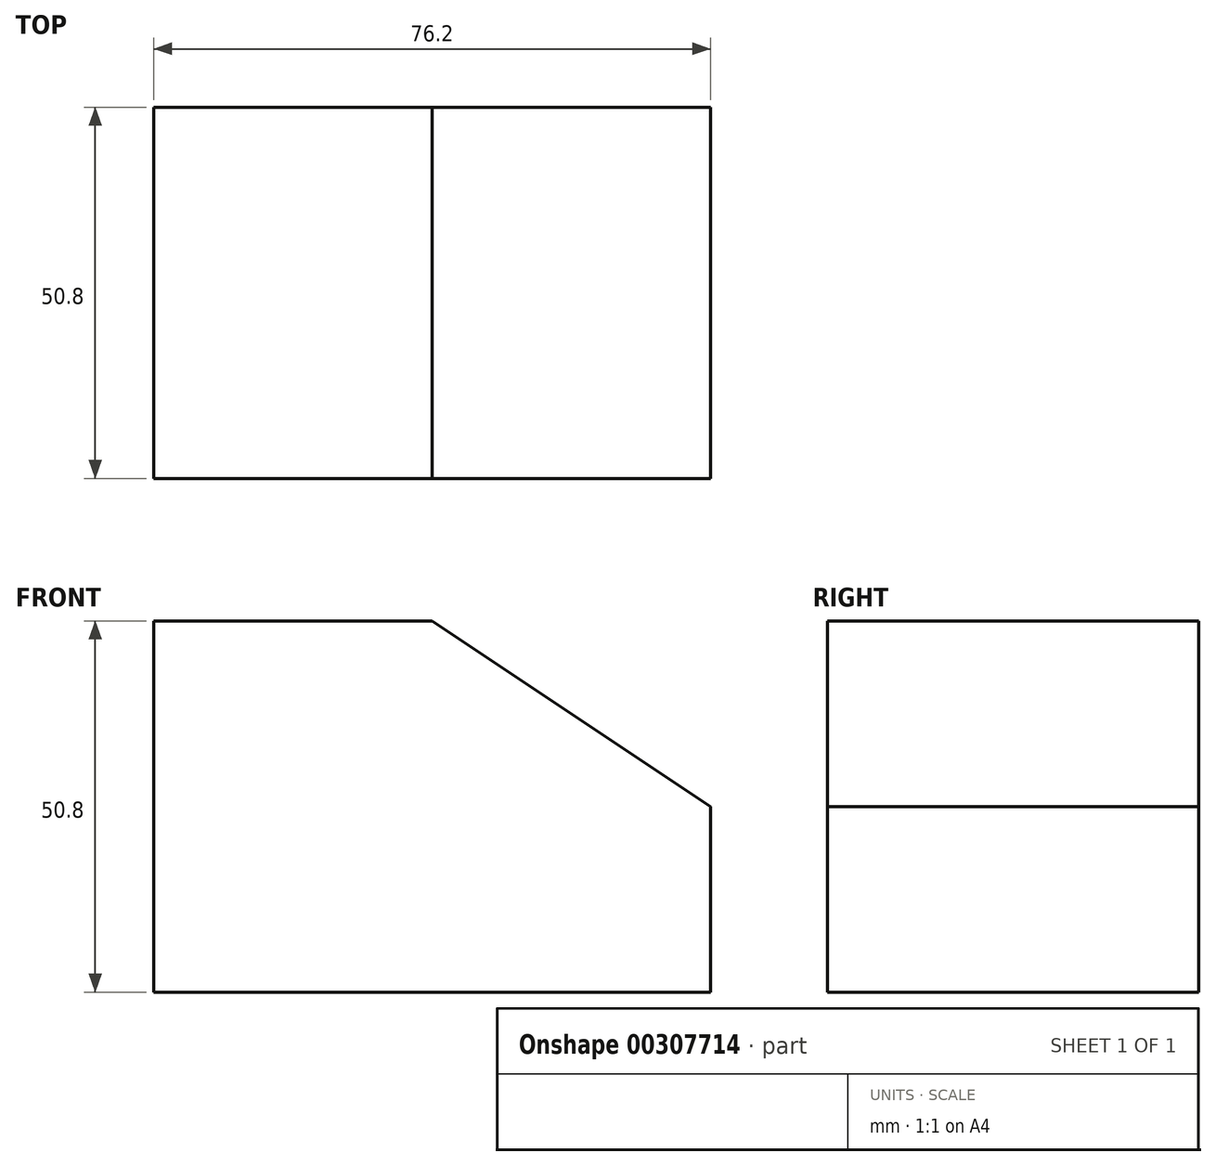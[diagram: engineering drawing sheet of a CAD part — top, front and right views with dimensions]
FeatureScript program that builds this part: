
annotation { "Feature Type Name" : "Feature", "Feature Type Description" : "" }
export const myFeature = defineFeature(function(context is Context, id is Id, definition is map)
    precondition{}
    {
        {
            var Q0;
            Q0=qCreatedBy(makeId("Front.planeOp"),FACE);
            var sketch = newSketch(context, id + "F0", { "sketchPlane" : qUnion([Q0])});
            skLineSegment(sketch, "E0", {"start": v(-37.96, -42.78) * mm, "end": v(38.24, -42.78) * mm});
            skLineSegment(sketch, "E1", {"start": v(38.24, -42.78) * mm, "end": v(38.24, -17.38) * mm});
            skLineSegment(sketch, "E2", {"start": v(-37.96, -42.78) * mm, "end": v(-37.96, 8.02) * mm});
            skLineSegment(sketch, "E3", {"start": v(-37.96, 8.02) * mm, "end": v(0.14, 8.02) * mm});
            skLineSegment(sketch, "E4", {"start": v(0.14, 8.02) * mm, "end": v(38.24, -17.38) * mm});
            skSolve(sketch);
        }
        {
            var Q0;
            Q0=makeQuery(id+"F0.imprint","IMPRINT",FACE,{"disambiguationData":[TD([[makeQuery(id+"F0.imprint","IMPRINT",EDGE,{"derivedFrom":sQuery(id+"F0.wireOp",EDGE,"E0")}),1.0]])]});
            extrude(context, id + "F1", {"entities" : qUnion([Q0]), "depth" : 50.8 * mm});
        }
    });
